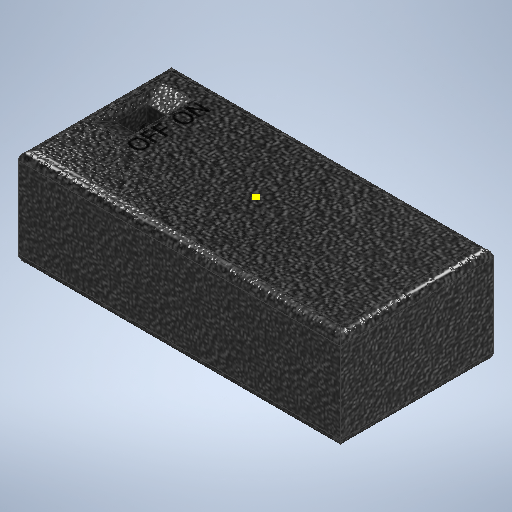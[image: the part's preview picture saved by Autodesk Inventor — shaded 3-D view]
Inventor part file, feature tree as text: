
AUTODESK INVENTOR PART (.ipt)
format: ipt  version: 2025.2 (Build 292293000, 293)  size: 399,872 bytes
history: native  units: in
note: dims shown in document units (in); Inventor stores cm internally (conversion verified against a paired STEP export)
features: draft x4, sketch x4, extrude x3, fillet x1
ambient origin geometry x8: Origin, YZ Plane, XZ Plane, XY Plane, X Axis, Y Axis, Z Axis, Center Point
bodies: Solid1 (feature_tree)
feature tree (12):
  extrude  "Extrusion1"  Depth=1.25in
  fillet  "Fillet1"  Radius=0.625in
  extrude  "Extrusion2"  Depth=0.8125in TaperAngle=0.0deg
  extrude  "Extrusion3"  Depth=0.25in
  draft  "FaceDraft1"
  draft  "FaceDraft2"
  draft  "FaceDraft3"
  draft  "FaceDraft4"
  sketch  "Sketch4"  dims[d8=0.5625in d9=0.1875in d10=0.25in d11=0.1565in d12=0.031in d13=0.1875in d14=0.0in d15=0.25in d16=0.5625in d17=0.1565in d19=0.0312in d20=0.0625in d21=0.0in d22=0.1855in d23=0.1855in d24=0.1512in d25=0.1512in]
  sketch  "Sketch1"  dims[d0=2.625in d1=1.25in d2=0.625in]
  sketch  "Sketch2"  dims[d3=1.3125in d4=0.8125in d5=0.0in]
  sketch  "Sketch3"  dims[d6=0.075in d7=0.25in]
